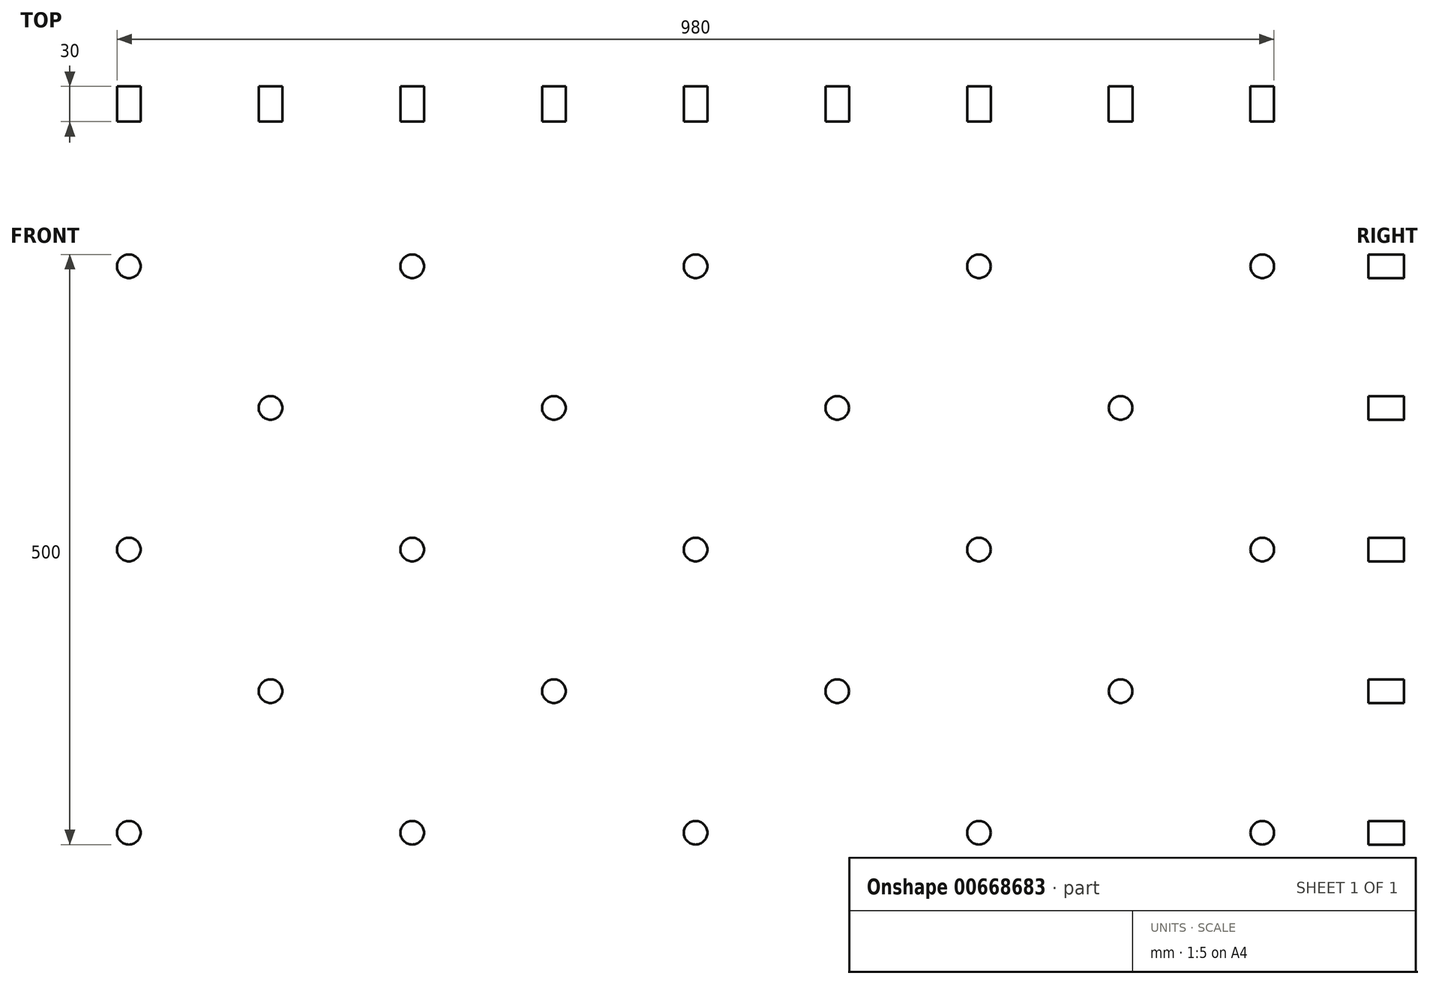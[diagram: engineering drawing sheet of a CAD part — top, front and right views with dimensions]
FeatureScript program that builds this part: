
annotation { "Feature Type Name" : "Feature", "Feature Type Description" : "" }
export const myFeature = defineFeature(function(context is Context, id is Id, definition is map)
    precondition{}
    {
        {
            assignVariable(context, id + "F0", {"name" : "SupportDepth", "anyValue" : 30});
        }
        {
            var Q0;
            Q0=qCreatedBy(makeId("Front.planeOp"),FACE);
            var sketch = newSketch(context, id + "F1", { "sketchPlane" : qUnion([Q0])});
            skCircle(sketch, "E0", {"center": v(-28.4, 12.4) * mm, "radius": 10 * mm});
            skLineSegment(sketch, "E1", {"start": v(0, 40.54) * mm, "end": v(0, -46.47) * mm, "construction": true});
            skCircle(sketch, "E2.0.1.0", {"center": v(-28.4, 132.4) * mm, "radius": 10 * mm});
            skCircle(sketch, "E2.0.2.0", {"center": v(-28.4, 252.4) * mm, "radius": 10 * mm});
            skCircle(sketch, "E2.0.3.0", {"center": v(-28.4, 372.4) * mm, "radius": 10 * mm});
            skCircle(sketch, "E2.0.4.0", {"center": v(-28.4, 492.4) * mm, "radius": 10 * mm});
            skCircle(sketch, "E2.1.0.0", {"center": v(91.6, 12.4) * mm, "radius": 10 * mm});
            skCircle(sketch, "E2.1.1.0", {"center": v(91.6, 132.4) * mm, "radius": 10 * mm});
            skCircle(sketch, "E2.1.2.0", {"center": v(91.6, 252.4) * mm, "radius": 10 * mm});
            skCircle(sketch, "E2.1.3.0", {"center": v(91.6, 372.4) * mm, "radius": 10 * mm});
            skCircle(sketch, "E2.1.4.0", {"center": v(91.6, 492.4) * mm, "radius": 10 * mm});
            skCircle(sketch, "E2.2.0.0", {"center": v(211.6, 12.4) * mm, "radius": 10 * mm});
            skCircle(sketch, "E2.2.1.0", {"center": v(211.6, 132.4) * mm, "radius": 10 * mm});
            skCircle(sketch, "E2.2.2.0", {"center": v(211.6, 252.4) * mm, "radius": 10 * mm});
            skCircle(sketch, "E2.2.3.0", {"center": v(211.6, 372.4) * mm, "radius": 10 * mm});
            skCircle(sketch, "E2.2.4.0", {"center": v(211.6, 492.4) * mm, "radius": 10 * mm});
            skCircle(sketch, "E2.3.0.0", {"center": v(331.6, 12.4) * mm, "radius": 10 * mm});
            skCircle(sketch, "E2.3.1.0", {"center": v(331.6, 132.4) * mm, "radius": 10 * mm});
            skCircle(sketch, "E2.3.2.0", {"center": v(331.6, 252.4) * mm, "radius": 10 * mm});
            skCircle(sketch, "E2.3.3.0", {"center": v(331.6, 372.4) * mm, "radius": 10 * mm});
            skCircle(sketch, "E2.3.4.0", {"center": v(331.6, 492.4) * mm, "radius": 10 * mm});
            skCircle(sketch, "E2.4.0.0", {"center": v(451.6, 12.4) * mm, "radius": 10 * mm});
            skCircle(sketch, "E2.4.1.0", {"center": v(451.6, 132.4) * mm, "radius": 10 * mm});
            skCircle(sketch, "E2.4.2.0", {"center": v(451.6, 252.4) * mm, "radius": 10 * mm});
            skCircle(sketch, "E2.4.3.0", {"center": v(451.6, 372.4) * mm, "radius": 10 * mm});
            skCircle(sketch, "E2.4.4.0", {"center": v(451.6, 492.4) * mm, "radius": 10 * mm});
            skCircle(sketch, "E2.5.0.0", {"center": v(571.6, 12.4) * mm, "radius": 10 * mm});
            skCircle(sketch, "E2.5.1.0", {"center": v(571.6, 132.4) * mm, "radius": 10 * mm});
            skCircle(sketch, "E2.5.2.0", {"center": v(571.6, 252.4) * mm, "radius": 10 * mm});
            skCircle(sketch, "E2.5.3.0", {"center": v(571.6, 372.4) * mm, "radius": 10 * mm});
            skCircle(sketch, "E2.5.4.0", {"center": v(571.6, 492.4) * mm, "radius": 10 * mm});
            skCircle(sketch, "E2.6.0.0", {"center": v(691.6, 12.4) * mm, "radius": 10 * mm});
            skCircle(sketch, "E2.6.1.0", {"center": v(691.6, 132.4) * mm, "radius": 10 * mm});
            skCircle(sketch, "E2.6.2.0", {"center": v(691.6, 252.4) * mm, "radius": 10 * mm});
            skCircle(sketch, "E2.6.3.0", {"center": v(691.6, 372.4) * mm, "radius": 10 * mm});
            skCircle(sketch, "E2.6.4.0", {"center": v(691.6, 492.4) * mm, "radius": 10 * mm});
            skCircle(sketch, "E2.7.0.0", {"center": v(811.6, 12.4) * mm, "radius": 10 * mm});
            skCircle(sketch, "E2.7.1.0", {"center": v(811.6, 132.4) * mm, "radius": 10 * mm});
            skCircle(sketch, "E2.7.2.0", {"center": v(811.6, 252.4) * mm, "radius": 10 * mm});
            skCircle(sketch, "E2.7.3.0", {"center": v(811.6, 372.4) * mm, "radius": 10 * mm});
            skCircle(sketch, "E2.7.4.0", {"center": v(811.6, 492.4) * mm, "radius": 10 * mm});
            skCircle(sketch, "E2.8.0.0", {"center": v(931.6, 12.4) * mm, "radius": 10 * mm});
            skCircle(sketch, "E2.8.1.0", {"center": v(931.6, 132.4) * mm, "radius": 10 * mm});
            skCircle(sketch, "E2.8.2.0", {"center": v(931.6, 252.4) * mm, "radius": 10 * mm});
            skCircle(sketch, "E2.8.3.0", {"center": v(931.6, 372.4) * mm, "radius": 10 * mm});
            skCircle(sketch, "E2.8.4.0", {"center": v(931.6, 492.4) * mm, "radius": 10 * mm});
            skCircle(sketch, "E2.9.0.0", {"center": v(1051.6, 12.4) * mm, "radius": 10 * mm});
            skCircle(sketch, "E2.9.1.0", {"center": v(1051.6, 132.4) * mm, "radius": 10 * mm});
            skCircle(sketch, "E2.9.2.0", {"center": v(1051.6, 252.4) * mm, "radius": 10 * mm});
            skCircle(sketch, "E2.9.3.0", {"center": v(1051.6, 372.4) * mm, "radius": 10 * mm});
            skCircle(sketch, "E2.9.4.0", {"center": v(1051.6, 492.4) * mm, "radius": 10 * mm});
            skLineSegment(sketch, "E2.direction1", {"start": v(-28.4, 12.4) * mm, "end": v(91.6, 12.4) * mm, "construction": true});
            skLineSegment(sketch, "E2.direction2", {"start": v(-28.4, 12.4) * mm, "end": v(-28.4, 132.4) * mm, "construction": true});
            skLineSegment(sketch, "E3", {"start": v(-35.46, 19.47) * mm, "end": v(444.54, 499.47) * mm, "construction": true});
            skSolve(sketch);
        }
        {
            var Q0;
            Q0 = qSketchRegion(id + "F1", true);
            extrude(context, id + "F2", {"entities" : qUnion([Q0]), "depth" : (getVariable(context, 'SupportDepth')) * mm, "offsetDistance" : 25 * mm});
        }
        {
            var Q0;
            Q0=makeQuery(id+"F2.opExtrude","SWEPT_BODY",BODY,{"disambiguationData":[OSD([sQuery(id+"F1.wireOp",EDGE,"E2.0.3.0")])]});
            var Q1;
            Q1=makeQuery(id+"F2.opExtrude","SWEPT_BODY",BODY,{"disambiguationData":[OSD([sQuery(id+"F1.wireOp",EDGE,"E2.1.4.0")])]});
            var Q2;
            Q2=makeQuery(id+"F2.opExtrude","SWEPT_BODY",BODY,{"disambiguationData":[OSD([sQuery(id+"F1.wireOp",EDGE,"E2.2.3.0")])]});
            var Q3;
            Q3=makeQuery(id+"F2.opExtrude","SWEPT_BODY",BODY,{"disambiguationData":[OSD([sQuery(id+"F1.wireOp",EDGE,"E2.1.2.0")])]});
            var Q4;
            Q4=makeQuery(id+"F2.opExtrude","SWEPT_BODY",BODY,{"disambiguationData":[OSD([sQuery(id+"F1.wireOp",EDGE,"E2.0.1.0")])]});
            var Q5;
            Q5=makeQuery(id+"F2.opExtrude","SWEPT_BODY",BODY,{"disambiguationData":[OSD([sQuery(id+"F1.wireOp",EDGE,"E2.3.4.0")])]});
            deleteBodies(context, id + "F3", {"entities" : qUnion([Q0, Q1, Q2, Q3, Q4, Q5])});
        }
        {
            var Q0;
            Q0=makeQuery(id+"F2.opExtrude","SWEPT_BODY",BODY,{"disambiguationData":[OSD([sQuery(id+"F1.wireOp",EDGE,"E2.1.0.0")])]});
            var Q1;
            Q1=makeQuery(id+"F2.opExtrude","SWEPT_BODY",BODY,{"disambiguationData":[OSD([sQuery(id+"F1.wireOp",EDGE,"E2.2.1.0")])]});
            var Q2;
            Q2=makeQuery(id+"F2.opExtrude","SWEPT_BODY",BODY,{"disambiguationData":[OSD([sQuery(id+"F1.wireOp",EDGE,"E2.3.2.0")])]});
            var Q3;
            Q3=makeQuery(id+"F2.opExtrude","SWEPT_BODY",BODY,{"disambiguationData":[OSD([sQuery(id+"F1.wireOp",EDGE,"E2.4.3.0")])]});
            var Q4;
            Q4=makeQuery(id+"F2.opExtrude","SWEPT_BODY",BODY,{"disambiguationData":[OSD([sQuery(id+"F1.wireOp",EDGE,"E2.5.4.0")])]});
            var Q5;
            Q5=makeQuery(id+"F2.opExtrude","SWEPT_BODY",BODY,{"disambiguationData":[OSD([sQuery(id+"F1.wireOp",EDGE,"E2.7.4.0")])]});
            var Q6;
            Q6=makeQuery(id+"F2.opExtrude","SWEPT_BODY",BODY,{"disambiguationData":[OSD([sQuery(id+"F1.wireOp",EDGE,"E2.6.3.0")])]});
            var Q7;
            Q7=makeQuery(id+"F2.opExtrude","SWEPT_BODY",BODY,{"disambiguationData":[OSD([sQuery(id+"F1.wireOp",EDGE,"E2.5.2.0")])]});
            var Q8;
            Q8=makeQuery(id+"F2.opExtrude","SWEPT_BODY",BODY,{"disambiguationData":[OSD([sQuery(id+"F1.wireOp",EDGE,"E2.4.1.0")])]});
            var Q9;
            Q9=makeQuery(id+"F2.opExtrude","SWEPT_BODY",BODY,{"disambiguationData":[OSD([sQuery(id+"F1.wireOp",EDGE,"E2.3.0.0")])]});
            var Q10;
            Q10=makeQuery(id+"F2.opExtrude","SWEPT_BODY",BODY,{"disambiguationData":[OSD([sQuery(id+"F1.wireOp",EDGE,"E2.5.0.0")])]});
            var Q11;
            Q11=makeQuery(id+"F2.opExtrude","SWEPT_BODY",BODY,{"disambiguationData":[OSD([sQuery(id+"F1.wireOp",EDGE,"E2.6.1.0")])]});
            var Q12;
            Q12=makeQuery(id+"F2.opExtrude","SWEPT_BODY",BODY,{"disambiguationData":[OSD([sQuery(id+"F1.wireOp",EDGE,"E2.7.2.0")])]});
            var Q13;
            Q13=makeQuery(id+"F2.opExtrude","SWEPT_BODY",BODY,{"disambiguationData":[OSD([sQuery(id+"F1.wireOp",EDGE,"E2.8.3.0")])]});
            var Q14;
            Q14=makeQuery(id+"F2.opExtrude","SWEPT_BODY",BODY,{"disambiguationData":[OSD([sQuery(id+"F1.wireOp",EDGE,"E2.9.4.0")])]});
            deleteBodies(context, id + "F4", {"entities" : qUnion([Q0, Q1, Q2, Q3, Q4, Q5, Q6, Q7, Q8, Q9, Q10, Q11, Q12, Q13, Q14])});
        }
        {
            var Q0;
            Q0=makeQuery(id+"F2.opExtrude","SWEPT_BODY",BODY,{"disambiguationData":[OSD([sQuery(id+"F1.wireOp",EDGE,"E2.7.0.0")])]});
            var Q1;
            Q1=makeQuery(id+"F2.opExtrude","SWEPT_BODY",BODY,{"disambiguationData":[OSD([sQuery(id+"F1.wireOp",EDGE,"E2.8.1.0")])]});
            deleteBodies(context, id + "F5", {"entities" : qUnion([Q0, Q1])});
        }
        {
            var Q0;
            Q0=makeQuery(id+"F2.opExtrude","SWEPT_BODY",BODY,{"disambiguationData":[OSD([sQuery(id+"F1.wireOp",EDGE,"E2.9.0.0")])]});
            var Q1;
            Q1=makeQuery(id+"F2.opExtrude","SWEPT_BODY",BODY,{"disambiguationData":[OSD([sQuery(id+"F1.wireOp",EDGE,"E2.9.1.0")])]});
            var Q2;
            Q2=makeQuery(id+"F2.opExtrude","SWEPT_BODY",BODY,{"disambiguationData":[OSD([sQuery(id+"F1.wireOp",EDGE,"E2.9.2.0")])]});
            var Q3;
            Q3=makeQuery(id+"F2.opExtrude","SWEPT_BODY",BODY,{"disambiguationData":[OSD([sQuery(id+"F1.wireOp",EDGE,"E2.9.3.0")])]});
            deleteBodies(context, id + "F6", {"entities" : qUnion([Q0, Q1, Q2, Q3])});
        }
        {
            var Q0;
            Q0=makeQuery(id+"F2.opExtrude","CAP_FACE",FACE,{"disambiguationData":[OSD([sQuery(id+"F1.wireOp",EDGE,"E0")])],"isStart":false});
            var Q1;
            Q1=sQuery(id+"F1.wireOp",EDGE,"E2.direction1");
            cPlane(context, id + "F7", {"entities" : qUnion([Q0, Q1]), "cplaneType" : CPlaneType.LINE_ANGLE, "offset" : 10 * mm, "angle" : 5 * degree, "width" : 150 * mm, "height" : 150 * mm});
        }
    });
